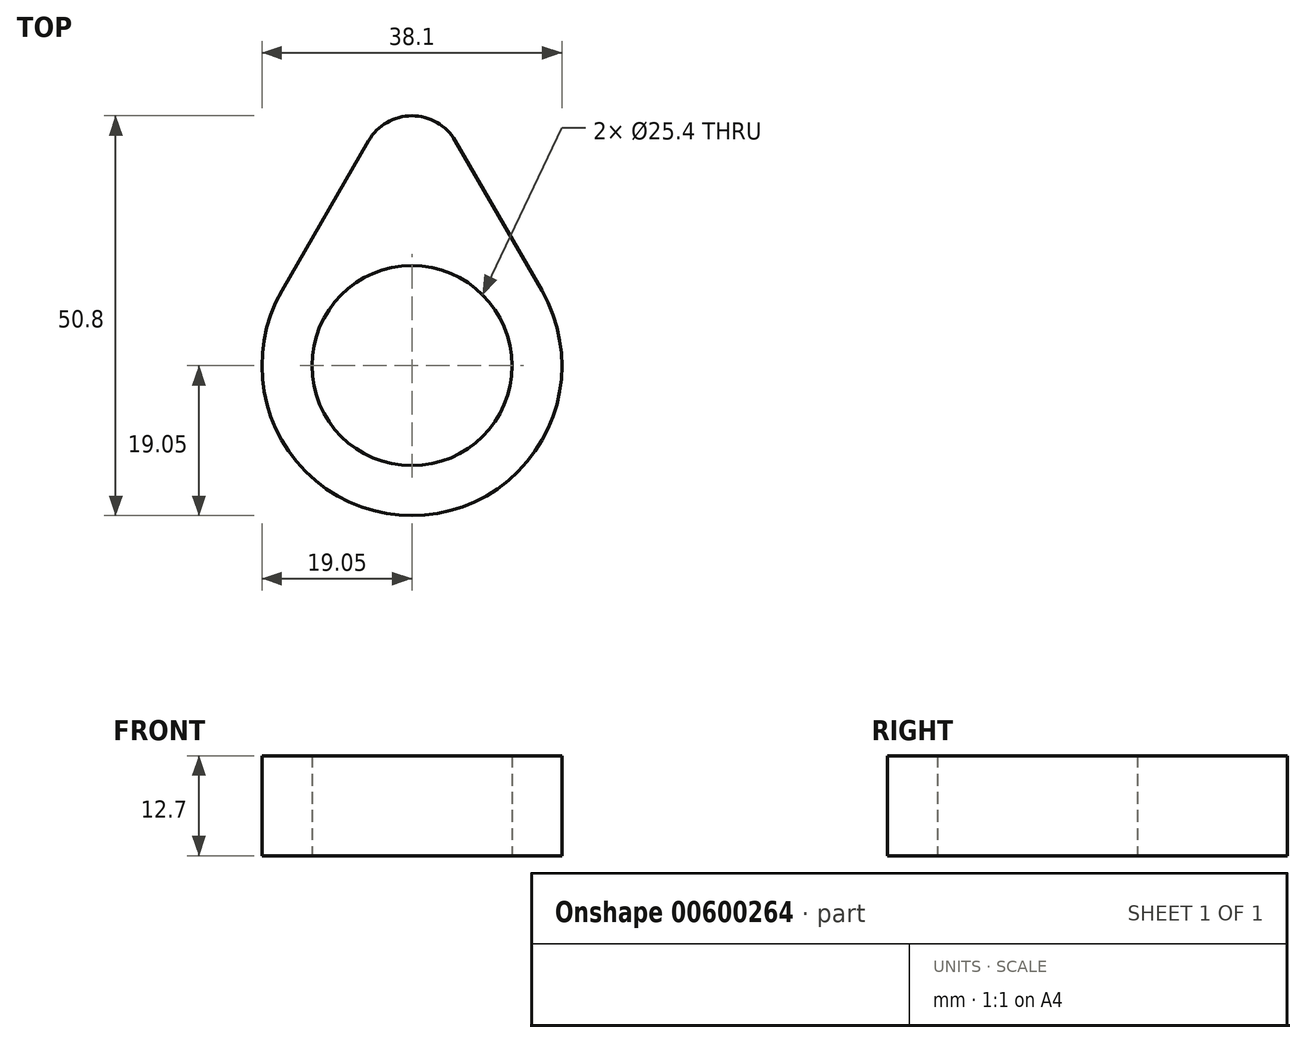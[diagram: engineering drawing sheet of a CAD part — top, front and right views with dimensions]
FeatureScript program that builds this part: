
annotation { "Feature Type Name" : "Feature", "Feature Type Description" : "" }
export const myFeature = defineFeature(function(context is Context, id is Id, definition is map)
    precondition{}
    {
        {
            var Q0;
            Q0=qCreatedBy(makeId("Top.planeOp"),FACE);
            var sketch = newSketch(context, id + "F0", { "sketchPlane" : qUnion([Q0])});
            skCircle(sketch, "E0", {"center": v(0, 0) * mm, "radius": 12.7 * mm});
            skArc(sketch, "E1", {"start": v(-16.5, 9.52) * mm, "mid": v(0, -19.05) * mm, "end": v(16.5, 9.52) * mm});
            skArc(sketch, "E2", {"start": v(5.5, 28.58) * mm, "mid": v(0, 31.75) * mm, "end": v(-5.5, 28.58) * mm});
            skLineSegment(sketch, "E3", {"start": v(16.5, 9.53) * mm, "end": v(5.5, 28.57) * mm});
            skLineSegment(sketch, "E4", {"start": v(-16.5, 9.53) * mm, "end": v(-5.5, 28.57) * mm});
            skSolve(sketch);
        }
        {
            var Q0;
            Q0 = qSketchRegion(id + "F0", true);
            extrude(context, id + "F1", {"entities" : qUnion([Q0]), "depth" : 12.7 * mm, "offsetDistance" : 25.4 * mm});
        }
    });
